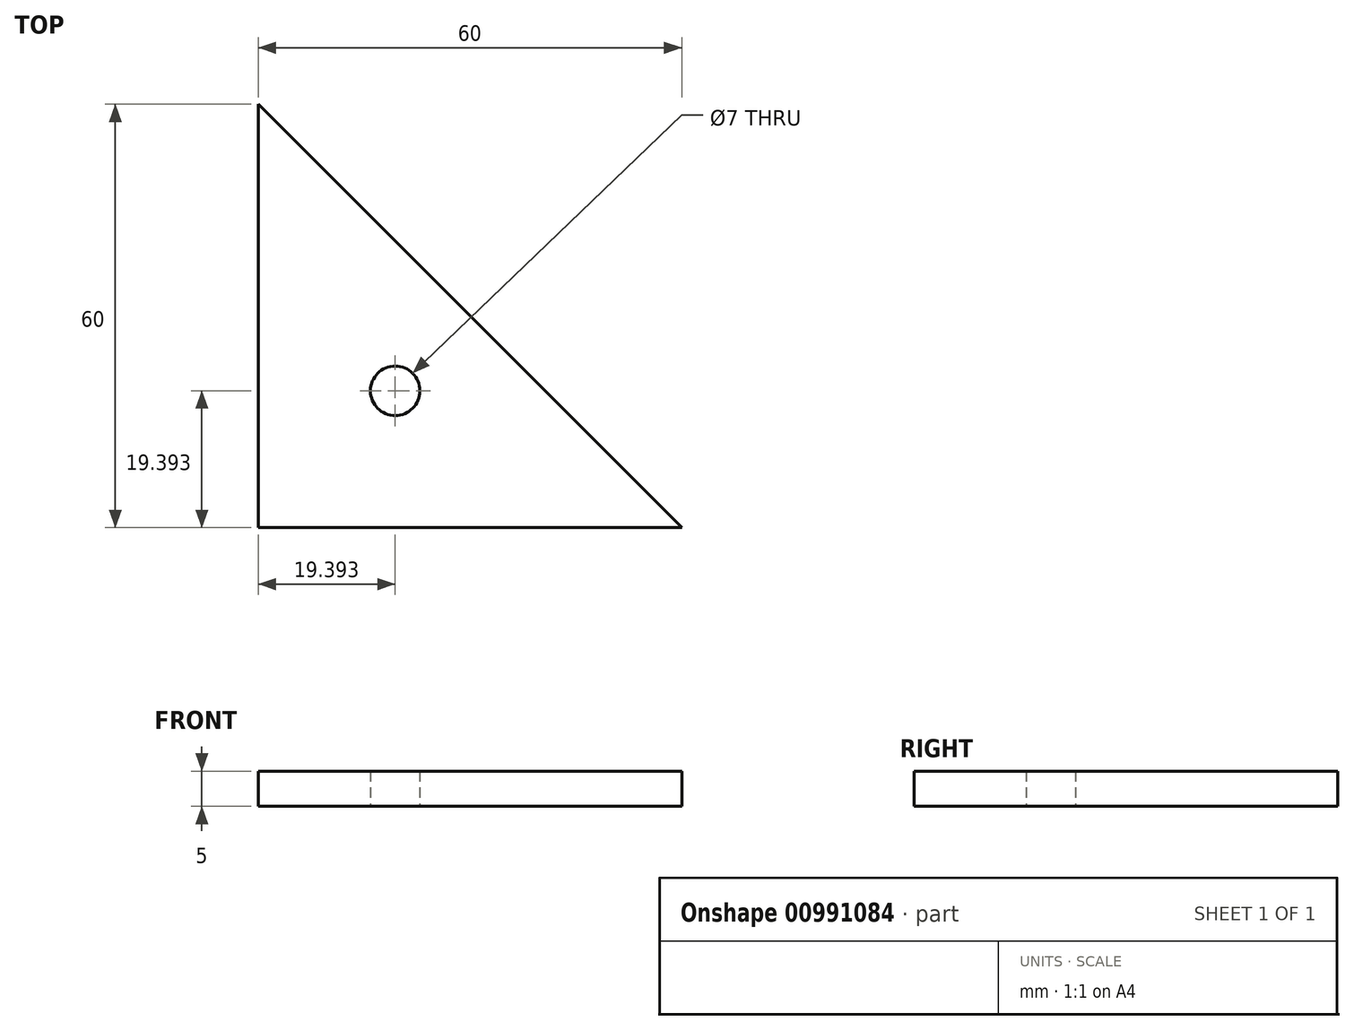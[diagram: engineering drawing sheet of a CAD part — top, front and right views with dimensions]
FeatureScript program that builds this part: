
annotation { "Feature Type Name" : "Feature", "Feature Type Description" : "" }
export const myFeature = defineFeature(function(context is Context, id is Id, definition is map)
    precondition{}
    {
        {
            var Q0;
            Q0=qCreatedBy(makeId("Top.planeOp"),FACE);
            var sketch = newSketch(context, id + "F0", { "sketchPlane" : qUnion([Q0])});
            skLineSegment(sketch, "E0", {"start": v(0, 0) * mm, "end": v(0, 60) * mm});
            skLineSegment(sketch, "E1", {"start": v(0, 0) * mm, "end": v(60, 0) * mm});
            skLineSegment(sketch, "E2", {"start": v(60, 0) * mm, "end": v(0, 60) * mm});
            skCircle(sketch, "E3", {"center": v(19.4, 19.4) * mm, "radius": 3.5 * mm});
            skLineSegment(sketch, "E4", {"start": v(30, 30) * mm, "end": v(19.4, 19.4) * mm});
            skSolve(sketch);
        }
        {
            var Q0;
            {var subQ1=sQuery(id+"F0.wireOp",EDGE,"E0");Q0=makeQuery(id+"F0.imprint","IMPRINT",FACE,{"disambiguationData":[TD([[makeQuery(id+"F0.imprint","IMPRINT",EDGE,{"derivedFrom":subQ1}),-1.0]])]});}
            extrude(context, id + "F1", {"entities" : qUnion([Q0]), "depth" : 5 * mm, "offsetDistance" : 25 * mm});
        }
    });
